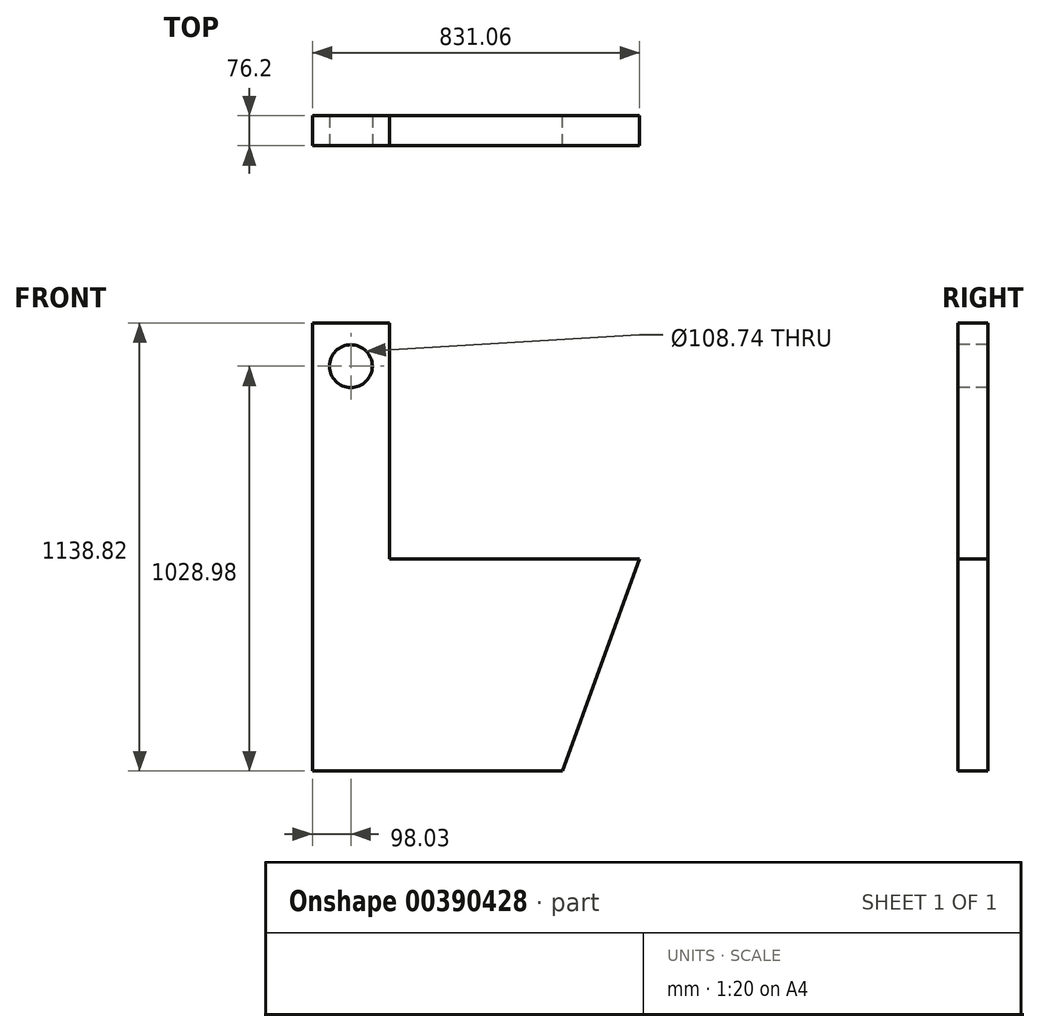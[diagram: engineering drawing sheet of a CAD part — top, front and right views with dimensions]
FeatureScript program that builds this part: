
annotation { "Feature Type Name" : "Feature", "Feature Type Description" : "" }
export const myFeature = defineFeature(function(context is Context, id is Id, definition is map)
    precondition{}
    {
        {
            var Q0;
            Q0=qCreatedBy(makeId("Front.planeOp"),FACE);
            var sketch = newSketch(context, id + "F0", { "sketchPlane" : qUnion([Q0])});
            skLineSegment(sketch, "E0", {"start": v(-196.06, 600.15) * mm, "end": v(-196.06, -538.67) * mm});
            skLineSegment(sketch, "E1", {"start": v(-196.06, -538.67) * mm, "end": v(438.94, -538.67) * mm});
            skLineSegment(sketch, "E2", {"start": v(438.94, -538.67) * mm, "end": v(635, 0) * mm});
            skLineSegment(sketch, "E3", {"start": v(635, 0) * mm, "end": v(0, 0) * mm});
            skLineSegment(sketch, "E4", {"start": v(0, 0) * mm, "end": v(0, 600.15) * mm});
            skLineSegment(sketch, "E5", {"start": v(0, 600.15) * mm, "end": v(-196.06, 600.15) * mm});
            skSolve(sketch);
        }
        {
            var Q0;
            Q0 = qSketchRegion(id + "F0", true);
            extrude(context, id + "F1", {"entities" : qUnion([Q0]), "depth" : 76.2 * mm});
        }
        {
            var Q0;
            Q0=makeQuery(id+"F1.opExtrude","CAP_FACE",FACE,{"disambiguationData":[OSD([sQuery(id+"F0.wireOp",EDGE,"E0"),sQuery(id+"F0.wireOp",EDGE,"E1"),sQuery(id+"F0.wireOp",EDGE,"E2"),sQuery(id+"F0.wireOp",EDGE,"E3"),sQuery(id+"F0.wireOp",EDGE,"E4"),sQuery(id+"F0.wireOp",EDGE,"E5")])],"isStart":false});
            var sketch = newSketch(context, id + "F2", { "sketchPlane" : qUnion([Q0])});
            skCircle(sketch, "E6", {"center": v(-98.03, 490.31) * mm, "radius": 54.37 * mm});
            skPoint(sketch, "E6.centerSnap0", {"position": v(-98.03, 600.15) * mm});
            skSolve(sketch);
        }
        {
            var Q0;
            Q0 = qSketchRegion(id + "F2", true);
            extrude(context, id + "F3", {"entities" : qUnion([Q0]), "operationType" : NewBodyOperationType.REMOVE, "oppositeDirection" : true, "depth" : 76.2 * mm});
        }
    });
